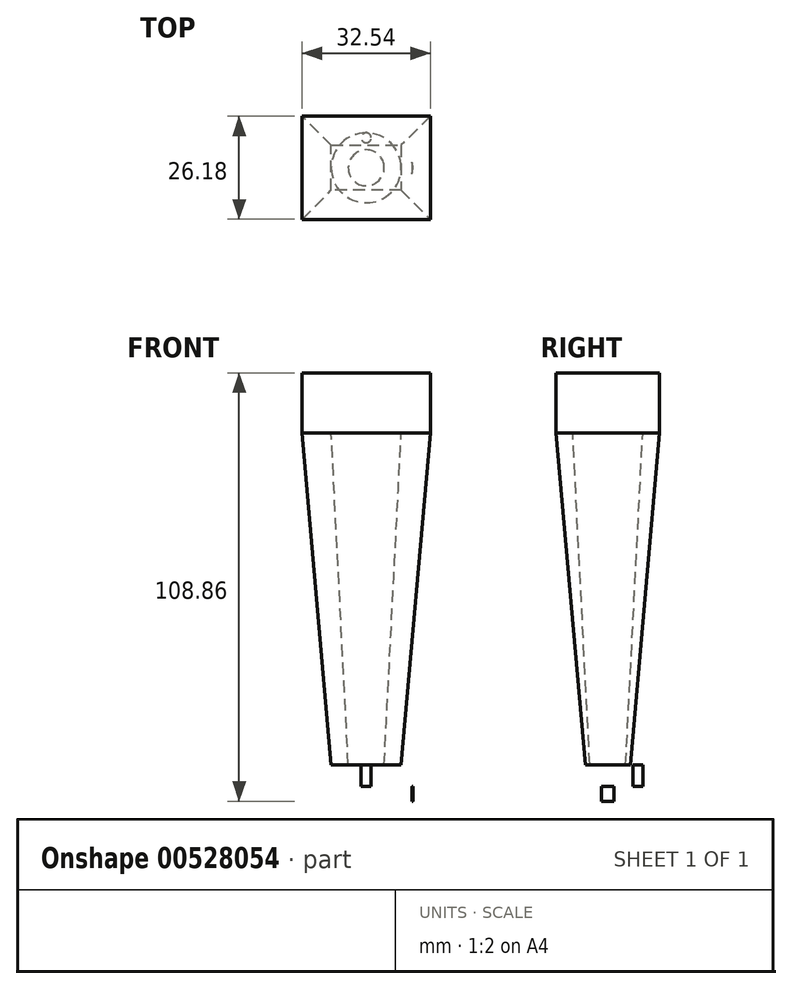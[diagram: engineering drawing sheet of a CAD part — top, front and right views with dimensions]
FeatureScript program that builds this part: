
annotation { "Feature Type Name" : "Feature", "Feature Type Description" : "" }
export const myFeature = defineFeature(function(context is Context, id is Id, definition is map)
    precondition{}
    {
        {
            var Q0;
            Q0=qCreatedBy(makeId("Top.planeOp"),FACE);
            var sketch = newSketch(context, id + "F0", { "sketchPlane" : qUnion([Q0])});
            skLineSegment(sketch, "E0", {"start": v(0, 0) * mm, "end": v(-6.15, 0) * mm, "construction": true});
            skLineSegment(sketch, "E1", {"start": v(0, 0) * mm, "end": v(5.9, 0) * mm, "construction": true});
            skArc(sketch, "E2", {"start": v(-3.08, 5.7) * mm, "mid": v(-12.62, 0) * mm, "end": v(-3.08, -5.7) * mm});
            skLineSegment(sketch, "E3", {"start": v(4.18, -5.7) * mm, "end": v(-3.08, -5.7) * mm});
            skLineSegment(sketch, "E4.MirrorCS", {"start": v(4.18, 5.7) * mm, "end": v(-3.08, 5.7) * mm});
            skArc(sketch, "E5.trimOffspring", {"start": v(4.18, -5.7) * mm, "mid": v(11.85, 0) * mm, "end": v(4.18, 5.7) * mm});
            skSolve(sketch);
        }
        {
            var Q0;
            {var subQ5=sQuery(id+"F0.wireOp",EDGE,"E2");Q0=makeQuery(id+"F0.imprint","IMPRINT",FACE,{"disambiguationData":[TD([[makeQuery(id+"F0.imprint","IMPRINT",EDGE,{"derivedFrom":subQ5}),1.0]])]});}
            extrude(context, id + "F1", {"entities" : qUnion([Q0]), "depth" : -3.8 * mm, "offsetDistance" : 25.4 * mm});
        }
        {
            var Q0;
            Q0=qCreatedBy(makeId("Top.planeOp"),FACE);
            var sketch = newSketch(context, id + "F2", { "sketchPlane" : qUnion([Q0])});
            skArc(sketch, "E6", {"start": v(-10.89, -4.41) * mm, "mid": v(11.75, 0) * mm, "end": v(-10.89, 4.41) * mm});
            skLineSegment(sketch, "E7", {"start": v(0, 0) * mm, "end": v(-6.15, 0) * mm, "construction": true});
            skArc(sketch, "E8", {"start": v(-10.89, 4.41) * mm, "mid": v(-12.62, 0) * mm, "end": v(-10.89, -4.41) * mm});
            skSolve(sketch);
        }
        {
            var Q0;
            Q0=makeQuery(id+"F2.imprint","IMPRINT",FACE,{"disambiguationData":[TD([[makeQuery(id+"F2.imprint","IMPRINT",EDGE,{"derivedFrom":sQuery(id+"F2.wireOp",EDGE,"E6")}),1.0]])]});
            extrude(context, id + "F3", {"entities" : qUnion([Q0]), "operationType" : NewBodyOperationType.ADD, "depth" : 5.46 * mm, "offsetDistance" : 25.4 * mm});
        }
        {
            var Q0;
            Q0=makeQuery(id+"F1.opExtrude","CAP_FACE",FACE,{"disambiguationData":[OSD([sQuery(id+"F0.wireOp",EDGE,"E2"),sQuery(id+"F0.wireOp",EDGE,"E3"),sQuery(id+"F0.wireOp",EDGE,"E4.MirrorCS"),sQuery(id+"F0.wireOp",EDGE,"E5.trimOffspring")])],"isStart":false});
            var sketch = newSketch(context, id + "F4", { "sketchPlane" : qUnion([Q0])});
            skCircle(sketch, "E9", {"center": v(0, 0) * mm, "radius": 5.08 * mm});
            skSolve(sketch);
        }
        {
            var Q0;
            Q0=makeQuery(id+"F3.opExtrude","CAP_FACE",FACE,{"disambiguationData":[OSD([sQuery(id+"F2.wireOp",EDGE,"E6"),sQuery(id+"F2.wireOp",EDGE,"E8")])],"isStart":false});
            var sketch = newSketch(context, id + "F5", { "sketchPlane" : qUnion([Q0])});
            skLineSegment(sketch, "E10", {"start": v(0, 0) * mm, "end": v(0, -7.62) * mm, "construction": true});
            skCircle(sketch, "E11", {"center": v(0, -7.62) * mm, "radius": 1.27 * mm});
            skCircle(sketch, "E12.MirrorC", {"center": v(0, 7.62) * mm, "radius": 1.27 * mm});
            skSolve(sketch);
        }
        {
            var Q0;
            Q0=makeQuery(id+"F5.imprint","IMPRINT",FACE,{"disambiguationData":[TD([[makeQuery(id+"F5.imprint","IMPRINT",EDGE,{"derivedFrom":sQuery(id+"F5.wireOp",EDGE,"E11")}),1.0]])]});
            var Q1;
            Q1=makeQuery(id+"F5.imprint","IMPRINT",FACE,{"disambiguationData":[TD([[makeQuery(id+"F5.imprint","IMPRINT",EDGE,{"derivedFrom":sQuery(id+"F5.wireOp",EDGE,"E12.MirrorC")}),-1.0]])]});
            extrude(context, id + "F6", {"entities" : qUnion([Q0, Q1]), "operationType" : NewBodyOperationType.REMOVE, "endBound" : BoundingType.THROUGH_ALL, "oppositeDirection" : true, "depth" : 10.16 * mm, "offsetDistance" : 25.4 * mm});
        }
        {
            var Q0;
            Q0=makeQuery(id+"F3.opExtrude","CAP_FACE",FACE,{"disambiguationData":[OSD([sQuery(id+"F2.wireOp",EDGE,"E6"),sQuery(id+"F2.wireOp",EDGE,"E8")])],"isStart":false});
            var sketch = newSketch(context, id + "F7", { "sketchPlane" : qUnion([Q0])});
            skLineSegment(sketch, "E13.bottom", {"start": v(8.9, -5.72) * mm, "end": v(-8.9, -5.72) * mm});
            skLineSegment(sketch, "E13.top", {"start": v(8.89, 5.72) * mm, "end": v(-8.89, 5.72) * mm});
            skLineSegment(sketch, "E13.left", {"start": v(8.9, -5.72) * mm, "end": v(8.9, 5.71) * mm});
            skLineSegment(sketch, "E13.right", {"start": v(-8.9, -5.72) * mm, "end": v(-8.9, 5.71) * mm});
            skPoint(sketch, "E13.middle", {"position": v(0, 0) * mm});
            skSolve(sketch);
        }
        {
            var Q0;
            Q0=makeQuery(id+"F7.imprint","IMPRINT",FACE,{"disambiguationData":[TD([[makeQuery(id+"F7.imprint","IMPRINT",EDGE,{"derivedFrom":sQuery(id+"F7.wireOp",EDGE,"E13.bottom")}),-1.0]])]});
            extrude(context, id + "F8", {"entities" : qUnion([Q0]), "operationType" : NewBodyOperationType.ADD, "depth" : 84.35 * mm, "offsetDistance" : 25.4 * mm, "hasDraft" : true, "draftAngle" : 5 * degree});
        }
        {
            var Q0;
            Q0=makeQuery(id+"F4.imprint","IMPRINT",FACE,{"disambiguationData":[TD([[makeQuery(id+"F4.imprint","IMPRINT",EDGE,{"derivedFrom":sQuery(id+"F4.wireOp",EDGE,"E9")}),-1.0]])]});
            var sketch = newSketch(context, id + "F9", { "sketchPlane" : qUnion([Q0])});
            skCircle(sketch, "E14", {"center": v(0, 0) * mm, "radius": 4.09 * mm});
            skSolve(sketch);
        }
        {
            var Q0;
            Q0=makeQuery(id+"F9.imprint","IMPRINT",FACE,{"disambiguationData":[TD([[makeQuery(id+"F9.imprint","IMPRINT",EDGE,{"derivedFrom":sQuery(id+"F9.wireOp",EDGE,"E14")}),1.0]])]});
            extrude(context, id + "F10", {"entities" : qUnion([Q0]), "operationType" : NewBodyOperationType.REMOVE, "endBound" : BoundingType.THROUGH_ALL, "oppositeDirection" : true, "depth" : 25.4 * mm, "offsetDistance" : 25.4 * mm, "hasDraft" : true, "draftAngle" : 2.94 * degree});
        }
        {
            var Q0;
            Q0=makeQuery(id+"F8.opExtrude","CAP_FACE",FACE,{"disambiguationData":[OSD([sQuery(id+"F7.wireOp",EDGE,"E13.bottom"),sQuery(id+"F7.wireOp",EDGE,"E13.top"),sQuery(id+"F7.wireOp",EDGE,"E13.left"),sQuery(id+"F7.wireOp",EDGE,"E13.right")])],"isStart":false});
            var sketch = newSketch(context, id + "F11", { "sketchPlane" : qUnion([Q0])});
            skLineSegment(sketch, "E15.bottom", {"start": v(-16.27, -13.1) * mm, "end": v(16.27, -13.1) * mm});
            skLineSegment(sketch, "E15.top", {"start": v(-16.27, 13.1) * mm, "end": v(16.27, 13.1) * mm});
            skLineSegment(sketch, "E15.left", {"start": v(-16.27, -13.1) * mm, "end": v(-16.27, 13.1) * mm});
            skLineSegment(sketch, "E15.right", {"start": v(16.27, -13.1) * mm, "end": v(16.27, 13.1) * mm});
            skSolve(sketch);
        }
        {
            var Q0;
            Q0 = qSketchRegion(id + "F11", true);
            extrude(context, id + "F12", {"entities" : qUnion([Q0]), "operationType" : NewBodyOperationType.ADD, "depth" : 15.24 * mm, "offsetDistance" : 25.4 * mm});
        }
        {
            var Q0;
            Q0=makeQuery(id+"F12.opExtrude","CAP_FACE",FACE,{"disambiguationData":[OSD([sQuery(id+"F11.wireOp",EDGE,"E15.bottom"),sQuery(id+"F11.wireOp",EDGE,"E15.top"),sQuery(id+"F11.wireOp",EDGE,"E15.left"),sQuery(id+"F11.wireOp",EDGE,"E15.right")])],"isStart":false});
            var sketch = newSketch(context, id + "F13", { "sketchPlane" : qUnion([Q0])});
            skCircle(sketch, "E16", {"center": v(0, 0) * mm, "radius": 9.5 * mm});
            skSolve(sketch);
        }
        {
            var Q0;
            Q0=sQuery(id+"F13.wireOp",VERTEX,"E16.center");
            var Q1;
            Q1=makeQuery(id+"F1.opExtrude","SWEPT_BODY",BODY,{"disambiguationData":[OSD([sQuery(id+"F0.wireOp",EDGE,"E2"),sQuery(id+"F0.wireOp",EDGE,"E3"),sQuery(id+"F0.wireOp",EDGE,"E4.MirrorCS"),sQuery(id+"F0.wireOp",EDGE,"E5.trimOffspring")])]});
            hole(context, id + "F14", {"style" : HoleStyle.SIMPLE, "endStyle" : HoleEndStyle.BLIND, "holeDiameter" : 19.94 * mm, "holeDepth" : 20.07 * mm, "isTappedThrough" : true, "tappedDepth" : 15.24 * mm, "tapClearance" : 3, "startFromSketch" : true, "locations" : qUnion([Q0]), "scope" : qUnion([Q1])});
        }
    });
